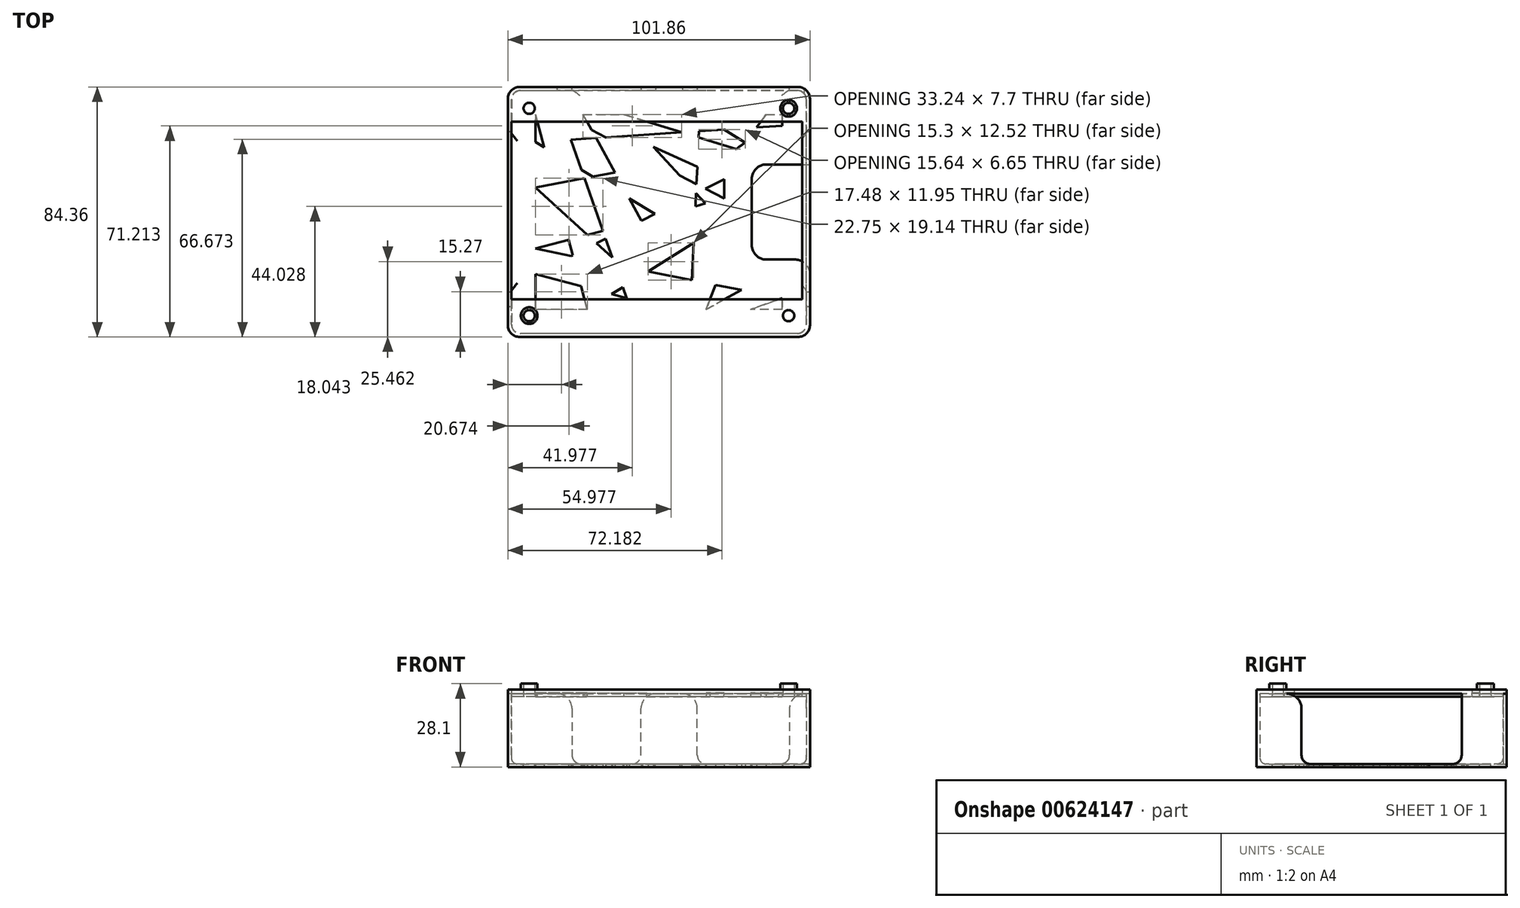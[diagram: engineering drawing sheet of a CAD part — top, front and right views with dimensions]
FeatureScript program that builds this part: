
annotation { "Feature Type Name" : "Feature", "Feature Type Description" : "" }
export const myFeature = defineFeature(function(context is Context, id is Id, definition is map)
    precondition{}
    {
        {
            var Q0;
            Q0=qCreatedBy(makeId("Top.planeOp"),FACE);
            var sketch = newSketch(context, id + "F0", { "sketchPlane" : qUnion([Q0])});
            skPoint(sketch, "E0.middle", {"position": v(0, 0) * mm});
            skLineSegment(sketch, "E1", {"start": v(0, 0) * mm, "end": v(0, -24.25) * mm, "construction": true});
            skLineSegment(sketch, "E2", {"start": v(0, 0) * mm, "end": v(-32.44, 0) * mm, "construction": true});
            skCircle(sketch, "E3", {"center": v(43.73, -34.98) * mm, "radius": 1.9 * mm});
            skCircle(sketch, "E4.MirrorC", {"center": v(-43.73, -34.98) * mm, "radius": 1.9 * mm});
            skCircle(sketch, "E5.MirrorC", {"center": v(-43.73, 34.98) * mm, "radius": 1.9 * mm});
            skCircle(sketch, "E6.MirrorC", {"center": v(43.73, 34.98) * mm, "radius": 1.9 * mm});
            skPoint(sketch, "E0.left.start.orphan", {"position": v(-50, 40) * mm});
            skPoint(sketch, "E0.top.start.orphan", {"position": v(-50, -40) * mm});
            skPoint(sketch, "E0.right.end.orphan", {"position": v(50, -40) * mm});
            skPoint(sketch, "E0.right.start.orphan", {"position": v(50, 40) * mm});
            skSolve(sketch);
        }
        {
            var Q0;
            Q0=qCreatedBy(makeId("Top.planeOp"),FACE);
            var sketch = newSketch(context, id + "F1", { "sketchPlane" : qUnion([Q0])});
            skPoint(sketch, "E7.0", {"position": v(-43.73, 34.98) * mm});
            skPoint(sketch, "E8.0", {"position": v(43.73, 34.98) * mm});
            skPoint(sketch, "E9.0", {"position": v(-43.73, -34.98) * mm});
            skPoint(sketch, "E10.0", {"position": v(43.73, -34.98) * mm});
            skLineSegment(sketch, "E11.0", {"start": v(-49.73, 40.98) * mm, "end": v(49.73, 40.98) * mm});
            skLineSegment(sketch, "E11.1", {"start": v(-49.73, -40.98) * mm, "end": v(-49.73, 40.98) * mm});
            skLineSegment(sketch, "E11.2", {"start": v(49.73, -40.98) * mm, "end": v(-49.73, -40.98) * mm});
            skLineSegment(sketch, "E11.3", {"start": v(49.73, 40.98) * mm, "end": v(49.73, -40.98) * mm});
            skLineSegment(sketch, "E12.0", {"start": v(-50.93, -42.18) * mm, "end": v(-50.93, 42.18) * mm});
            skLineSegment(sketch, "E12.1", {"start": v(50.93, -42.18) * mm, "end": v(-50.93, -42.18) * mm});
            skLineSegment(sketch, "E12.2", {"start": v(50.93, 42.18) * mm, "end": v(50.93, -42.18) * mm});
            skLineSegment(sketch, "E12.3", {"start": v(-50.93, 42.18) * mm, "end": v(50.93, 42.18) * mm});
            skSolve(sketch);
        }
        {
            var Q0;
            Q0=makeQuery(id+"F1.imprint","IMPRINT",FACE,{"disambiguationData":[TD([[makeQuery(id+"F1.imprint","IMPRINT",EDGE,{"derivedFrom":sQuery(id+"F1.wireOp",EDGE,"E11.0")}),-1.0]])]});
            var Q1;
            Q1=makeQuery(id+"F1.imprint","IMPRINT",FACE,{"disambiguationData":[TD([[makeQuery(id+"F1.imprint","IMPRINT",EDGE,{"derivedFrom":sQuery(id+"F1.wireOp",EDGE,"E11.0")}),1.0]])]});
            extrude(context, id + "F2", {"entities" : qUnion([Q0, Q1]), "oppositeDirection" : true, "depth" : 1 * mm, "offsetDistance" : 25 * mm});
        }
        {
            var Q0;
            Q0=makeQuery(id+"F1.imprint","IMPRINT",FACE,{"disambiguationData":[TD([[makeQuery(id+"F1.imprint","IMPRINT",EDGE,{"derivedFrom":sQuery(id+"F1.wireOp",EDGE,"E11.0")}),1.0]])]});
            extrude(context, id + "F3", {"entities" : qUnion([Q0]), "operationType" : NewBodyOperationType.ADD, "depth" : 23.7 * mm, "offsetDistance" : 25 * mm});
        }
        {
            var Q0;
            {var subQ0=sQuery(id+"F1.wireOp",EDGE,"E12.0");Q0=makeQuery(id+"F3.boolean.opBoolean","MERGE",FACE,{"derivedFrom":[makeQuery(id+"F2.opExtrude","SWEPT_FACE",FACE,{"disambiguationData":[OSD([subQ0])]}),makeQuery(id+"F3.opExtrude","SWEPT_FACE",FACE,{"disambiguationData":[OSD([subQ0])]})]});}
            var sketch = newSketch(context, id + "F4", { "sketchPlane" : qUnion([Q0])});
            skLineSegment(sketch, "E13", {"start": v(0, 0) * mm, "end": v(0, 24.76) * mm, "construction": true});
            skPoint(sketch, "E14.0", {"position": v(-40.98, 0) * mm});
            skPoint(sketch, "E15.0", {"position": v(40.98, 23.7) * mm});
            skPoint(sketch, "E16.0", {"position": v(40.98, 0) * mm});
            skPoint(sketch, "E17.0", {"position": v(-40.98, 23.7) * mm});
            skLineSegment(sketch, "E18", {"start": v(-40.98, 23.7) * mm, "end": v(40.98, 0) * mm, "construction": true});
            skLineSegment(sketch, "E19", {"start": v(40.98, 23.7) * mm, "end": v(-40.98, 0) * mm, "construction": true});
            skLineSegment(sketch, "E20.bottom", {"start": v(27, 0) * mm, "end": v(-27, 0) * mm});
            skLineSegment(sketch, "E20.top", {"start": v(27, 24.76) * mm, "end": v(-27, 24.76) * mm});
            skLineSegment(sketch, "E20.left", {"start": v(27, 0) * mm, "end": v(27, 24.76) * mm});
            skLineSegment(sketch, "E20.right", {"start": v(-27, 0) * mm, "end": v(-27, 24.76) * mm});
            skPoint(sketch, "E20.middle", {"position": v(0, 12.38) * mm});
            skSolve(sketch);
        }
        {
            var Q0;
            {var subQ0=sQuery(id+"F4.wireOp",EDGE,"E20.bottom");Q0=makeQuery(id+"F4.imprint","IMPRINT",FACE,{"disambiguationData":[TD([[makeQuery(id+"F4.imprint","IMPRINT",EDGE,{"derivedFrom":subQ0}),-1.0]])]});}
            extrude(context, id + "F5", {"entities" : qUnion([Q0]), "operationType" : NewBodyOperationType.REMOVE, "endBound" : BoundingType.THROUGH_ALL, "oppositeDirection" : true, "depth" : 25 * mm, "offsetDistance" : 25 * mm});
        }
        {
            var Q0;
            {var subQ0=sQuery(id+"F1.wireOp",EDGE,"E12.3");Q0=makeQuery(id+"F3.boolean.opBoolean","MERGE",FACE,{"derivedFrom":[makeQuery(id+"F2.opExtrude","SWEPT_FACE",FACE,{"disambiguationData":[OSD([subQ0])]}),makeQuery(id+"F3.opExtrude","SWEPT_FACE",FACE,{"disambiguationData":[OSD([subQ0])]})]});}
            var sketch = newSketch(context, id + "F6", { "sketchPlane" : qUnion([Q0])});
            skLineSegment(sketch, "E21", {"start": v(-50.93, 11.35) * mm, "end": v(-12.93, 11.35) * mm, "construction": true});
            skLineSegment(sketch, "E22", {"start": v(-50.93, 7.6) * mm, "end": v(6.07, 7.6) * mm, "construction": true});
            skLineSegment(sketch, "E23", {"start": v(-12.93, 11.35) * mm, "end": v(-12.93, 25.37) * mm});
            skLineSegment(sketch, "E24", {"start": v(-12.93, 25.37) * mm, "end": v(-44.03, 25.37) * mm});
            skLineSegment(sketch, "E25", {"start": v(-44.03, 25.37) * mm, "end": v(-44.03, 0) * mm});
            skLineSegment(sketch, "E26", {"start": v(-44.03, 0) * mm, "end": v(-12.93, 0) * mm});
            skLineSegment(sketch, "E27", {"start": v(-12.93, 0) * mm, "end": v(-12.93, 11.35) * mm});
            skLineSegment(sketch, "E28", {"start": v(6.07, 7.6) * mm, "end": v(6.07, 25.85) * mm});
            skLineSegment(sketch, "E29", {"start": v(6.07, 25.85) * mm, "end": v(29.28, 25.85) * mm});
            skLineSegment(sketch, "E30", {"start": v(29.28, 25.85) * mm, "end": v(29.28, 0) * mm});
            skLineSegment(sketch, "E31", {"start": v(29.28, 0) * mm, "end": v(6.07, 0) * mm});
            skLineSegment(sketch, "E32", {"start": v(6.07, 0) * mm, "end": v(6.07, 7.6) * mm});
            skSolve(sketch);
        }
        {
            var Q0;
            Q0 = qSketchRegion(id + "F6", true);
            extrude(context, id + "F7", {"entities" : qUnion([Q0]), "operationType" : NewBodyOperationType.REMOVE, "oppositeDirection" : true, "depth" : 25 * mm, "offsetDistance" : 25 * mm});
        }
        {
            var Q0;
            Q0=makeQuery(id+"F0.imprint","IMPRINT",FACE,{"disambiguationData":[TD([[makeQuery(id+"F0.imprint","IMPRINT",EDGE,{"derivedFrom":sQuery(id+"F0.wireOp",EDGE,"E6.MirrorC")}),-1.0]])]});
            var Q1;
            Q1=makeQuery(id+"F0.imprint","IMPRINT",FACE,{"disambiguationData":[TD([[makeQuery(id+"F0.imprint","IMPRINT",EDGE,{"derivedFrom":sQuery(id+"F0.wireOp",EDGE,"E3")}),1.0]])]});
            var Q2;
            Q2=makeQuery(id+"F0.imprint","IMPRINT",FACE,{"disambiguationData":[TD([[makeQuery(id+"F0.imprint","IMPRINT",EDGE,{"derivedFrom":sQuery(id+"F0.wireOp",EDGE,"E5.MirrorC")}),1.0]])]});
            var Q3;
            Q3=makeQuery(id+"F0.imprint","IMPRINT",FACE,{"disambiguationData":[TD([[makeQuery(id+"F0.imprint","IMPRINT",EDGE,{"derivedFrom":sQuery(id+"F0.wireOp",EDGE,"E4.MirrorC")}),-1.0]])]});
            extrude(context, id + "F8", {"entities" : qUnion([Q0, Q1, Q2, Q3]), "operationType" : NewBodyOperationType.REMOVE, "oppositeDirection" : true, "depth" : 25 * mm, "offsetDistance" : 25 * mm});
        }
        {
            var Q0;
            Q0=makeQuery(id+"F3.opExtrude","SWEPT_EDGE",EDGE,{"disambiguationData":[OSD([sQuery(id+"F1.wireOp",EDGE,"E11.2"),sQuery(id+"F1.wireOp",EDGE,"E11.3")])]});
            var Q1;
            Q1=makeQuery(id+"F3.opExtrude","SWEPT_EDGE",EDGE,{"disambiguationData":[OSD([sQuery(id+"F1.wireOp",EDGE,"E11.1"),sQuery(id+"F1.wireOp",EDGE,"E11.2")])]});
            var Q2;
            Q2=makeQuery(id+"F3.opExtrude","SWEPT_EDGE",EDGE,{"disambiguationData":[OSD([sQuery(id+"F1.wireOp",EDGE,"E11.0"),sQuery(id+"F1.wireOp",EDGE,"E11.1")])]});
            var Q3;
            Q3=makeQuery(id+"F3.opExtrude","SWEPT_EDGE",EDGE,{"disambiguationData":[OSD([sQuery(id+"F1.wireOp",EDGE,"E11.0"),sQuery(id+"F1.wireOp",EDGE,"E11.3")])]});
            fillet(context, id + "F9", {"entities" : qUnion([Q0, Q1, Q2, Q3]), "radius" : 3 * mm, "tangentPropagation" : true, "allowEdgeOverflow" : false});
        }
        {
            var Q0;
            {var subQ0=sQuery(id+"F1.wireOp",EDGE,"E12.3");var subQ1=sQuery(id+"F1.wireOp",EDGE,"E12.0");Q0=makeQuery(id+"F3.boolean.opBoolean","MERGE",EDGE,{"derivedFrom":[makeQuery(id+"F2.opExtrude","SWEPT_EDGE",EDGE,{"disambiguationData":[OSD([subQ1,subQ0])]}),makeQuery(id+"F3.opExtrude","SWEPT_EDGE",EDGE,{"disambiguationData":[OSD([subQ1,subQ0])]})]});}
            var Q1;
            {var subQ0=sQuery(id+"F1.wireOp",EDGE,"E12.1");var subQ1=sQuery(id+"F1.wireOp",EDGE,"E12.0");Q1=makeQuery(id+"F3.boolean.opBoolean","MERGE",EDGE,{"derivedFrom":[makeQuery(id+"F2.opExtrude","SWEPT_EDGE",EDGE,{"disambiguationData":[OSD([subQ1,subQ0])]}),makeQuery(id+"F3.opExtrude","SWEPT_EDGE",EDGE,{"disambiguationData":[OSD([subQ1,subQ0])]})]});}
            var Q2;
            {var subQ0=sQuery(id+"F1.wireOp",EDGE,"E12.2");var subQ1=sQuery(id+"F1.wireOp",EDGE,"E12.1");Q2=makeQuery(id+"F3.boolean.opBoolean","MERGE",EDGE,{"derivedFrom":[makeQuery(id+"F2.opExtrude","SWEPT_EDGE",EDGE,{"disambiguationData":[OSD([subQ1,subQ0])]}),makeQuery(id+"F3.opExtrude","SWEPT_EDGE",EDGE,{"disambiguationData":[OSD([subQ1,subQ0])]})]});}
            var Q3;
            {var subQ0=sQuery(id+"F1.wireOp",EDGE,"E12.3");var subQ1=sQuery(id+"F1.wireOp",EDGE,"E12.2");Q3=makeQuery(id+"F3.boolean.opBoolean","MERGE",EDGE,{"derivedFrom":[makeQuery(id+"F2.opExtrude","SWEPT_EDGE",EDGE,{"disambiguationData":[OSD([subQ1,subQ0])]}),makeQuery(id+"F3.opExtrude","SWEPT_EDGE",EDGE,{"disambiguationData":[OSD([subQ1,subQ0])]})]});}
            fillet(context, id + "F10", {"entities" : qUnion([Q0, Q1, Q2, Q3]), "radius" : 4 * mm, "tangentPropagation" : true, "allowEdgeOverflow" : false});
        }
        {
            var Q0;
            {var subQ0=sQuery(id+"F1.wireOp",EDGE,"E12.0");var subQ1=sQuery(id+"F4.wireOp",EDGE,"E20.bottom");var subQ2=sQuery(id+"F4.wireOp",EDGE,"E20.right");Q0=makeQuery(id+"F5.boolean.opBoolean","COPY",EDGE,{"disambiguationData":[TD([makeQuery(id+"F2.opExtrude","SWEPT_FACE",FACE,{"disambiguationData":[OSD([subQ0])]})])],"derivedFrom":makeQuery(id+"F5.opExtrude","SWEPT_EDGE",EDGE,{"disambiguationData":[OSD([subQ1,subQ2])]})});}
            var Q1;
            Q1=makeQuery(id+"F7.boolean.opBoolean","COPY",EDGE,{"derivedFrom":makeQuery(id+"F7.opExtrude","SWEPT_EDGE",EDGE,{"disambiguationData":[OSD([sQuery(id+"F6.wireOp",EDGE,"E30"),sQuery(id+"F6.wireOp",EDGE,"E31")])]})});
            var Q2;
            Q2=makeQuery(id+"F7.boolean.opBoolean","COPY",EDGE,{"derivedFrom":makeQuery(id+"F7.opExtrude","SWEPT_EDGE",EDGE,{"disambiguationData":[OSD([sQuery(id+"F6.wireOp",EDGE,"E31"),sQuery(id+"F6.wireOp",EDGE,"E32")])]})});
            var Q3;
            Q3=makeQuery(id+"F7.boolean.opBoolean","COPY",EDGE,{"derivedFrom":makeQuery(id+"F7.opExtrude","SWEPT_EDGE",EDGE,{"disambiguationData":[OSD([sQuery(id+"F6.wireOp",EDGE,"E26"),sQuery(id+"F6.wireOp",EDGE,"E27")])]})});
            var Q4;
            Q4=makeQuery(id+"F7.boolean.opBoolean","COPY",EDGE,{"derivedFrom":makeQuery(id+"F7.opExtrude","SWEPT_EDGE",EDGE,{"disambiguationData":[OSD([sQuery(id+"F6.wireOp",EDGE,"E25"),sQuery(id+"F6.wireOp",EDGE,"E26")])]})});
            var Q5;
            {var subQ0=sQuery(id+"F1.wireOp",EDGE,"E12.2");var subQ1=sQuery(id+"F4.wireOp",EDGE,"E20.bottom");var subQ2=sQuery(id+"F4.wireOp",EDGE,"E20.right");Q5=makeQuery(id+"F5.boolean.opBoolean","COPY",EDGE,{"disambiguationData":[TD([makeQuery(id+"F2.opExtrude","SWEPT_FACE",FACE,{"disambiguationData":[OSD([subQ0])]})])],"derivedFrom":makeQuery(id+"F5.opExtrude","SWEPT_EDGE",EDGE,{"disambiguationData":[OSD([subQ1,subQ2])]})});}
            var Q6;
            {var subQ0=sQuery(id+"F1.wireOp",EDGE,"E12.2");var subQ1=sQuery(id+"F4.wireOp",EDGE,"E20.left");var subQ2=sQuery(id+"F4.wireOp",EDGE,"E20.bottom");Q6=makeQuery(id+"F5.boolean.opBoolean","COPY",EDGE,{"disambiguationData":[TD([makeQuery(id+"F2.opExtrude","SWEPT_FACE",FACE,{"disambiguationData":[OSD([subQ0])]})])],"derivedFrom":makeQuery(id+"F5.opExtrude","SWEPT_EDGE",EDGE,{"disambiguationData":[OSD([subQ2,subQ1])]})});}
            var Q7;
            {var subQ0=sQuery(id+"F1.wireOp",EDGE,"E12.0");var subQ1=sQuery(id+"F4.wireOp",EDGE,"E20.left");var subQ2=sQuery(id+"F4.wireOp",EDGE,"E20.bottom");Q7=makeQuery(id+"F5.boolean.opBoolean","COPY",EDGE,{"disambiguationData":[TD([makeQuery(id+"F2.opExtrude","SWEPT_FACE",FACE,{"disambiguationData":[OSD([subQ0])]})])],"derivedFrom":makeQuery(id+"F5.opExtrude","SWEPT_EDGE",EDGE,{"disambiguationData":[OSD([subQ2,subQ1])]})});}
            fillet(context, id + "F11", {"entities" : qUnion([Q0, Q1, Q2, Q3, Q4, Q5, Q6, Q7]), "radius" : 3 * mm, "tangentPropagation" : true, "allowEdgeOverflow" : false});
        }
        {
            var Q0;
            {var subQ1=sQuery(id+"F1.wireOp",EDGE,"E12.2");var subQ2=sQuery(id+"F1.wireOp",EDGE,"E12.0");var subQ3=sQuery(id+"F4.wireOp",EDGE,"E20.left");Q0=makeQuery(id+"F5.boolean.opBoolean","COPY",EDGE,{"disambiguationData":[TD([makeQuery(id+"F2.opExtrude","SWEPT_FACE",FACE,{"disambiguationData":[OSD([subQ1])]})])],"derivedFrom":makeQuery(id+"F5.opExtrude","SWEPT_EDGE",EDGE,{"disambiguationData":[OSD([subQ2,subQ3])]})});}
            var Q1;
            {var subQ1=sQuery(id+"F1.wireOp",EDGE,"E12.2");var subQ2=sQuery(id+"F1.wireOp",EDGE,"E12.0");var subQ3=sQuery(id+"F4.wireOp",EDGE,"E20.right");Q1=makeQuery(id+"F5.boolean.opBoolean","COPY",EDGE,{"disambiguationData":[TD([makeQuery(id+"F2.opExtrude","SWEPT_FACE",FACE,{"disambiguationData":[OSD([subQ1])]})])],"derivedFrom":makeQuery(id+"F5.opExtrude","SWEPT_EDGE",EDGE,{"disambiguationData":[OSD([subQ2,subQ3])]})});}
            var Q2;
            {var subQ0=sQuery(id+"F1.wireOp",EDGE,"E11.0");var subQ1=sQuery(id+"F1.wireOp",EDGE,"E12.2");var subQ2=sQuery(id+"F1.wireOp",EDGE,"E12.3");var subQ3=sQuery(id+"F1.wireOp",EDGE,"E12.0");var subQ4=sQuery(id+"F1.wireOp",EDGE,"E11.1");var subQ5=sQuery(id+"F1.wireOp",EDGE,"E11.3");Q2=makeQuery(id+"F7.boolean.opBoolean","INTERSECT",EDGE,{"derivedFrom":[makeQuery(id+"F5.boolean.opBoolean","SPLIT",FACE,{"disambiguationData":[TD([makeQuery(id+"F2.opExtrude","SWEPT_FACE",FACE,{"disambiguationData":[OSD([subQ2])]})])],"derivedFrom":makeQuery(id+"F3.opExtrude","CAP_FACE",FACE,{"disambiguationData":[OSD([subQ0,subQ4,sQuery(id+"F1.wireOp",EDGE,"E11.2"),subQ5,subQ3,sQuery(id+"F1.wireOp",EDGE,"E12.1"),subQ1,subQ2])],"isStart":false})}),makeQuery(id+"F7.opExtrude","SWEPT_FACE",FACE,{"disambiguationData":[OSD([sQuery(id+"F6.wireOp",EDGE,"E25")])]})]});}
            var Q3;
            {var subQ0=sQuery(id+"F1.wireOp",EDGE,"E11.0");var subQ1=sQuery(id+"F1.wireOp",EDGE,"E12.2");var subQ2=sQuery(id+"F1.wireOp",EDGE,"E12.3");var subQ3=sQuery(id+"F1.wireOp",EDGE,"E12.0");var subQ4=sQuery(id+"F1.wireOp",EDGE,"E11.1");var subQ5=sQuery(id+"F1.wireOp",EDGE,"E11.3");Q3=makeQuery(id+"F7.boolean.opBoolean","INTERSECT",EDGE,{"derivedFrom":[makeQuery(id+"F5.boolean.opBoolean","SPLIT",FACE,{"disambiguationData":[TD([makeQuery(id+"F2.opExtrude","SWEPT_FACE",FACE,{"disambiguationData":[OSD([subQ2])]})])],"derivedFrom":makeQuery(id+"F3.opExtrude","CAP_FACE",FACE,{"disambiguationData":[OSD([subQ0,subQ4,sQuery(id+"F1.wireOp",EDGE,"E11.2"),subQ5,subQ3,sQuery(id+"F1.wireOp",EDGE,"E12.1"),subQ1,subQ2])],"isStart":false})}),makeQuery(id+"F7.opExtrude","SWEPT_FACE",FACE,{"disambiguationData":[OSD([sQuery(id+"F6.wireOp",EDGE,"E23"),sQuery(id+"F6.wireOp",EDGE,"E27")])]})]});}
            var Q4;
            {var subQ0=sQuery(id+"F1.wireOp",EDGE,"E11.0");var subQ1=sQuery(id+"F1.wireOp",EDGE,"E12.2");var subQ2=sQuery(id+"F1.wireOp",EDGE,"E12.3");var subQ3=sQuery(id+"F1.wireOp",EDGE,"E12.0");var subQ4=sQuery(id+"F1.wireOp",EDGE,"E11.1");var subQ5=sQuery(id+"F1.wireOp",EDGE,"E11.3");Q4=makeQuery(id+"F7.boolean.opBoolean","INTERSECT",EDGE,{"derivedFrom":[makeQuery(id+"F5.boolean.opBoolean","SPLIT",FACE,{"disambiguationData":[TD([makeQuery(id+"F2.opExtrude","SWEPT_FACE",FACE,{"disambiguationData":[OSD([subQ2])]})])],"derivedFrom":makeQuery(id+"F3.opExtrude","CAP_FACE",FACE,{"disambiguationData":[OSD([subQ0,subQ4,sQuery(id+"F1.wireOp",EDGE,"E11.2"),subQ5,subQ3,sQuery(id+"F1.wireOp",EDGE,"E12.1"),subQ1,subQ2])],"isStart":false})}),makeQuery(id+"F7.opExtrude","SWEPT_FACE",FACE,{"disambiguationData":[OSD([sQuery(id+"F6.wireOp",EDGE,"E28"),sQuery(id+"F6.wireOp",EDGE,"E32")])]})]});}
            var Q5;
            {var subQ0=sQuery(id+"F1.wireOp",EDGE,"E11.0");var subQ1=sQuery(id+"F1.wireOp",EDGE,"E12.2");var subQ2=sQuery(id+"F1.wireOp",EDGE,"E12.3");var subQ3=sQuery(id+"F1.wireOp",EDGE,"E12.0");var subQ4=sQuery(id+"F1.wireOp",EDGE,"E11.1");var subQ5=sQuery(id+"F1.wireOp",EDGE,"E11.3");Q5=makeQuery(id+"F7.boolean.opBoolean","INTERSECT",EDGE,{"derivedFrom":[makeQuery(id+"F5.boolean.opBoolean","SPLIT",FACE,{"disambiguationData":[TD([makeQuery(id+"F2.opExtrude","SWEPT_FACE",FACE,{"disambiguationData":[OSD([subQ2])]})])],"derivedFrom":makeQuery(id+"F3.opExtrude","CAP_FACE",FACE,{"disambiguationData":[OSD([subQ0,subQ4,sQuery(id+"F1.wireOp",EDGE,"E11.2"),subQ5,subQ3,sQuery(id+"F1.wireOp",EDGE,"E12.1"),subQ1,subQ2])],"isStart":false})}),makeQuery(id+"F7.opExtrude","SWEPT_FACE",FACE,{"disambiguationData":[OSD([sQuery(id+"F6.wireOp",EDGE,"E30")])]})]});}
            var Q6;
            {var subQ0=sQuery(id+"F1.wireOp",EDGE,"E12.0");var subQ2=sQuery(id+"F4.wireOp",EDGE,"E20.right");Q6=makeQuery(id+"F5.boolean.opBoolean","COPY",EDGE,{"disambiguationData":[TD([makeQuery(id+"F2.opExtrude","SWEPT_FACE",FACE,{"disambiguationData":[OSD([subQ0])]})])],"derivedFrom":makeQuery(id+"F5.opExtrude","SWEPT_EDGE",EDGE,{"disambiguationData":[OSD([subQ0,subQ2])]})});}
            var Q7;
            {var subQ0=sQuery(id+"F1.wireOp",EDGE,"E12.0");var subQ2=sQuery(id+"F4.wireOp",EDGE,"E20.left");Q7=makeQuery(id+"F5.boolean.opBoolean","COPY",EDGE,{"disambiguationData":[TD([makeQuery(id+"F2.opExtrude","SWEPT_FACE",FACE,{"disambiguationData":[OSD([subQ0])]})])],"derivedFrom":makeQuery(id+"F5.opExtrude","SWEPT_EDGE",EDGE,{"disambiguationData":[OSD([subQ0,subQ2])]})});}
            fillet(context, id + "F12", {"entities" : qUnion([Q0, Q1, Q2, Q3, Q4, Q5, Q6, Q7]), "radius" : 5 * mm, "tangentPropagation" : true, "allowEdgeOverflow" : false});
        }
        {
            var Q0;
            Q0=makeQuery(id+"F2.opExtrude","CAP_FACE",FACE,{"disambiguationData":[OSD([sQuery(id+"F1.wireOp",EDGE,"E12.0"),sQuery(id+"F1.wireOp",EDGE,"E12.1"),sQuery(id+"F1.wireOp",EDGE,"E12.2"),sQuery(id+"F1.wireOp",EDGE,"E12.3")])],"isStart":false});
            var sketch = newSketch(context, id + "F13", { "sketchPlane" : qUnion([Q0])});
            skLineSegment(sketch, "E33.top", {"start": v(50.93, 16.06) * mm, "end": v(31.3, 16.06) * mm});
            skLineSegment(sketch, "E33.left", {"start": v(50.93, 0) * mm, "end": v(50.93, 16.06) * mm});
            skLineSegment(sketch, "E33.right", {"start": v(31.3, 0) * mm, "end": v(31.3, 16.06) * mm});
            skLineSegment(sketch, "E34.MirrorCS", {"start": v(50.93, 0) * mm, "end": v(50.93, -16.06) * mm});
            skLineSegment(sketch, "E35.MirrorCS", {"start": v(50.93, -16.06) * mm, "end": v(31.3, -16.06) * mm});
            skLineSegment(sketch, "E36.MirrorCS", {"start": v(31.3, 0) * mm, "end": v(31.3, -16.06) * mm});
            skSolve(sketch);
        }
        {
            var Q0;
            Q0=makeQuery(id+"F13.imprint","IMPRINT",FACE,{"disambiguationData":[TD([[makeQuery(id+"F13.imprint","IMPRINT",EDGE,{"derivedFrom":sQuery(id+"F13.wireOp",EDGE,"E33.top")}),1.0]])]});
            extrude(context, id + "F14", {"entities" : qUnion([Q0]), "operationType" : NewBodyOperationType.REMOVE, "oppositeDirection" : true, "depth" : 25 * mm, "offsetDistance" : 25 * mm});
        }
        {
            var Q0;
            Q0=makeQuery(id+"F14.boolean.opBoolean","COPY",EDGE,{"derivedFrom":makeQuery(id+"F14.opExtrude","SWEPT_EDGE",EDGE,{"disambiguationData":[OSD([sQuery(id+"F1.wireOp",EDGE,"E12.2"),sQuery(id+"F13.wireOp",EDGE,"E33.top"),sQuery(id+"F13.wireOp",EDGE,"E33.left")])]})});
            var Q1;
            Q1=makeQuery(id+"F14.boolean.opBoolean","COPY",EDGE,{"derivedFrom":makeQuery(id+"F14.opExtrude","SWEPT_EDGE",EDGE,{"disambiguationData":[OSD([sQuery(id+"F1.wireOp",EDGE,"E12.2"),sQuery(id+"F13.wireOp",EDGE,"E34.MirrorCS"),sQuery(id+"F13.wireOp",EDGE,"E35.MirrorCS")])]})});
            var Q2;
            Q2=makeQuery(id+"F14.boolean.opBoolean","COPY",EDGE,{"derivedFrom":makeQuery(id+"F14.opExtrude","SWEPT_EDGE",EDGE,{"disambiguationData":[OSD([sQuery(id+"F13.wireOp",EDGE,"E33.top"),sQuery(id+"F13.wireOp",EDGE,"E33.right")])]})});
            var Q3;
            Q3=makeQuery(id+"F14.boolean.opBoolean","COPY",EDGE,{"derivedFrom":makeQuery(id+"F14.opExtrude","SWEPT_EDGE",EDGE,{"disambiguationData":[OSD([sQuery(id+"F13.wireOp",EDGE,"E35.MirrorCS"),sQuery(id+"F13.wireOp",EDGE,"E36.MirrorCS")])]})});
            fillet(context, id + "F15", {"entities" : qUnion([Q0, Q1, Q2, Q3]), "radius" : 5 * mm, "tangentPropagation" : true, "allowEdgeOverflow" : false});
        }
        {
            var Q0;
            Q0=qCreatedBy(makeId("Top.planeOp"),FACE);
            cPlane(context, id + "F16", {"entities" : qUnion([Q0]), "cplaneType" : CPlaneType.OFFSET, "offset" : 23.7 * mm, "width" : 150 * mm, "height" : 150 * mm});
        }
        {
            var Q0;
            Q0=qCreatedBy(id+"F16.planeOp",FACE);
            var sketch = newSketch(context, id + "F17", { "sketchPlane" : qUnion([Q0])});
            skLineSegment(sketch, "E37.0", {"start": v(50.93, -32) * mm, "end": v(50.93, -38.18) * mm});
            skArc(sketch, "E38.0", {"start": v(46.93, -42.18) * mm, "mid": v(49.76, -41.01) * mm, "end": v(50.93, -38.18) * mm});
            skLineSegment(sketch, "E39.0", {"start": v(46.93, -42.18) * mm, "end": v(-46.93, -42.18) * mm});
            skArc(sketch, "E40.0", {"start": v(-50.93, -38.18) * mm, "mid": v(-49.76, -41.01) * mm, "end": v(-46.93, -42.18) * mm});
            skLineSegment(sketch, "E41.0", {"start": v(-50.93, -38.18) * mm, "end": v(-50.93, -32) * mm});
            skLineSegment(sketch, "E42.0", {"start": v(-49.73, -37.98) * mm, "end": v(-49.73, -32) * mm});
            skArc(sketch, "E43.0", {"start": v(-46.73, -40.98) * mm, "mid": v(-48.85, -40.1) * mm, "end": v(-49.73, -37.98) * mm});
            skLineSegment(sketch, "E44.0", {"start": v(46.73, -40.98) * mm, "end": v(-46.73, -40.98) * mm});
            skArc(sketch, "E45.0", {"start": v(49.73, -37.98) * mm, "mid": v(48.85, -40.1) * mm, "end": v(46.73, -40.98) * mm});
            skLineSegment(sketch, "E46.0", {"start": v(49.73, -32) * mm, "end": v(49.73, -37.98) * mm});
            skLineSegment(sketch, "E47.0", {"start": v(49.73, 37.98) * mm, "end": v(49.73, 32) * mm});
            skLineSegment(sketch, "E48.0", {"start": v(50.93, 38.18) * mm, "end": v(50.93, 32) * mm});
            skArc(sketch, "E49.0", {"start": v(49.03, 39.9) * mm, "mid": v(49.55, 39) * mm, "end": v(49.73, 37.98) * mm});
            skArc(sketch, "E50.0", {"start": v(49.03, 39.9) * mm, "mid": v(48, 40.7) * mm, "end": v(46.73, 40.98) * mm});
            skLineSegment(sketch, "E51.0", {"start": v(46.73, 40.98) * mm, "end": v(44.03, 40.98) * mm});
            skLineSegment(sketch, "E52.0", {"start": v(44.03, 42.18) * mm, "end": v(46.93, 42.18) * mm});
            skArc(sketch, "E53.0", {"start": v(49.03, 41.58) * mm, "mid": v(48.02, 42.03) * mm, "end": v(46.93, 42.18) * mm});
            skArc(sketch, "E54.0", {"start": v(50.93, 38.18) * mm, "mid": v(50.42, 40.13) * mm, "end": v(49.03, 41.58) * mm});
            skLineSegment(sketch, "E55.0", {"start": v(50.93, 32) * mm, "end": v(50.93, 27) * mm});
            skLineSegment(sketch, "E56.0", {"start": v(49.73, 27) * mm, "end": v(49.73, 32) * mm});
            skLineSegment(sketch, "E57.0", {"start": v(-46.73, 40.98) * mm, "end": v(-34.28, 40.98) * mm});
            skLineSegment(sketch, "E58.0", {"start": v(-46.93, 42.18) * mm, "end": v(-34.28, 42.18) * mm});
            skArc(sketch, "E59.0", {"start": v(-46.93, 42.18) * mm, "mid": v(-49.76, 41.01) * mm, "end": v(-50.93, 38.18) * mm});
            skArc(sketch, "E60.0", {"start": v(-49.73, 37.98) * mm, "mid": v(-48.85, 40.1) * mm, "end": v(-46.73, 40.98) * mm});
            skLineSegment(sketch, "E61.0", {"start": v(-49.73, 32) * mm, "end": v(-49.73, 37.98) * mm});
            skLineSegment(sketch, "E62.0", {"start": v(-50.93, 32) * mm, "end": v(-50.93, 38.18) * mm});
            skLineSegment(sketch, "E63", {"start": v(49.73, -32) * mm, "end": v(49.73, 27) * mm});
            skLineSegment(sketch, "E64", {"start": v(50.93, -32) * mm, "end": v(50.93, 27) * mm});
            skLineSegment(sketch, "E65", {"start": v(44.03, 40.98) * mm, "end": v(-34.28, 40.98) * mm});
            skLineSegment(sketch, "E66", {"start": v(44.03, 42.18) * mm, "end": v(-34.28, 42.18) * mm});
            skLineSegment(sketch, "E67", {"start": v(-49.73, 32) * mm, "end": v(-49.73, -32) * mm});
            skLineSegment(sketch, "E68", {"start": v(-50.93, 32) * mm, "end": v(-50.93, -32) * mm});
            skCircle(sketch, "E69.0", {"center": v(-43.73, -34.98) * mm, "radius": 1.9 * mm});
            skCircle(sketch, "E70.0", {"center": v(-43.73, 34.98) * mm, "radius": 1.9 * mm});
            skCircle(sketch, "E71.0", {"center": v(43.73, -34.98) * mm, "radius": 1.9 * mm});
            skCircle(sketch, "E72.0", {"center": v(43.73, 34.98) * mm, "radius": 1.9 * mm});
            skLineSegment(sketch, "E73", {"start": v(43.73, 34.98) * mm, "end": v(43.73, 30.48) * mm, "construction": true});
            skLineSegment(sketch, "E74", {"start": v(43.73, 30.48) * mm, "end": v(48.29, 30.48) * mm, "construction": true});
            skLineSegment(sketch, "E75", {"start": v(48.29, 30.48) * mm, "end": v(-49.73, 30.48) * mm});
            skLineSegment(sketch, "E76", {"start": v(-49.73, 30.48) * mm, "end": v(-49.73, -29.52) * mm});
            skLineSegment(sketch, "E77", {"start": v(-49.73, -29.52) * mm, "end": v(48.29, -29.52) * mm});
            skLineSegment(sketch, "E78", {"start": v(48.29, -29.52) * mm, "end": v(48.29, 30.48) * mm});
            skSolve(sketch);
        }
        {
            var Q0;
            {var subQ2=sQuery(id+"F17.wireOp",EDGE,"E42.0");Q0=makeQuery(id+"F17.imprint","IMPRINT",FACE,{"disambiguationData":[TD([[makeQuery(id+"F17.imprint","IMPRINT",EDGE,{"derivedFrom":subQ2}),-1.0]])]});}
            var Q1;
            Q1=makeQuery(id+"F17.imprint","IMPRINT",FACE,{"disambiguationData":[TD([[makeQuery(id+"F17.imprint","IMPRINT",EDGE,{"derivedFrom":sQuery(id+"F17.wireOp",EDGE,"E37.0")}),-1.0]])]});
            extrude(context, id + "F18", {"entities" : qUnion([Q0, Q1]), "depth" : 3.4 * mm, "offsetDistance" : 25 * mm});
        }
        {
            var Q0;
            {var subQ2=sQuery(id+"F17.wireOp",EDGE,"E42.0");Q0=makeQuery(id+"F17.imprint","IMPRINT",FACE,{"disambiguationData":[TD([[makeQuery(id+"F17.imprint","IMPRINT",EDGE,{"derivedFrom":subQ2}),-1.0]])]});}
            extrude(context, id + "F19", {"entities" : qUnion([Q0]), "operationType" : NewBodyOperationType.ADD, "oppositeDirection" : true, "depth" : 1 * mm, "offsetDistance" : 25 * mm, "hasDraft" : true, "draftAngle" : 4 * degree, "draftPullDirection" : true});
        }
        {
            var Q0;
            Q0=makeQuery(id+"F18.opExtrude","CAP_FACE",FACE,{"disambiguationData":[OSD([sQuery(id+"F17.wireOp",EDGE,"E37.0"),sQuery(id+"F17.wireOp",EDGE,"E38.0"),sQuery(id+"F17.wireOp",EDGE,"E39.0"),sQuery(id+"F17.wireOp",EDGE,"E40.0"),sQuery(id+"F17.wireOp",EDGE,"E41.0"),sQuery(id+"F17.wireOp",EDGE,"E48.0"),sQuery(id+"F17.wireOp",EDGE,"E52.0"),sQuery(id+"F17.wireOp",EDGE,"E53.0"),sQuery(id+"F17.wireOp",EDGE,"E54.0"),sQuery(id+"F17.wireOp",EDGE,"E55.0"),sQuery(id+"F17.wireOp",EDGE,"E58.0"),sQuery(id+"F17.wireOp",EDGE,"E59.0"),sQuery(id+"F17.wireOp",EDGE,"E62.0"),sQuery(id+"F17.wireOp",EDGE,"E64"),sQuery(id+"F17.wireOp",EDGE,"E66"),sQuery(id+"F17.wireOp",EDGE,"E68"),sQuery(id+"F17.wireOp",EDGE,"E69.0"),sQuery(id+"F17.wireOp",EDGE,"E70.0"),sQuery(id+"F17.wireOp",EDGE,"E71.0"),sQuery(id+"F17.wireOp",EDGE,"E72.0"),sQuery(id+"F17.wireOp",EDGE,"E75"),sQuery(id+"F17.wireOp",EDGE,"E76"),sQuery(id+"F17.wireOp",EDGE,"E77"),sQuery(id+"F17.wireOp",EDGE,"E78")])],"isStart":false});
            var sketch = newSketch(context, id + "F20", { "sketchPlane" : qUnion([Q0])});
            skCircle(sketch, "E79", {"center": v(-43.73, 34.98) * mm, "radius": 2.8 * mm});
            skLineSegment(sketch, "E80", {"start": v(0, 0) * mm, "end": v(0, 13.28) * mm, "construction": true});
            skLineSegment(sketch, "E81", {"start": v(0, 0) * mm, "end": v(-20.42, 0) * mm, "construction": true});
            skCircle(sketch, "E82.MirrorC", {"center": v(43.73, 34.98) * mm, "radius": 2.8 * mm});
            skCircle(sketch, "E83.MirrorC", {"center": v(-43.73, -34.98) * mm, "radius": 2.8 * mm});
            skCircle(sketch, "E84.MirrorC", {"center": v(43.73, -34.98) * mm, "radius": 2.8 * mm});
            skSolve(sketch);
        }
        {
            var Q0;
            Q0=makeQuery(id+"F20.imprint","IMPRINT",FACE,{"disambiguationData":[TD([[makeQuery(id+"F20.imprint","IMPRINT",EDGE,{"derivedFrom":sQuery(id+"F20.wireOp",EDGE,"E79")}),1.0]])]});
            var Q1;
            Q1=makeQuery(id+"F20.imprint","IMPRINT",FACE,{"disambiguationData":[TD([[makeQuery(id+"F20.imprint","IMPRINT",EDGE,{"derivedFrom":sQuery(id+"F20.wireOp",EDGE,"E82.MirrorC")}),-1.0]])]});
            var Q2;
            Q2=makeQuery(id+"F20.imprint","IMPRINT",FACE,{"disambiguationData":[TD([[makeQuery(id+"F20.imprint","IMPRINT",EDGE,{"derivedFrom":sQuery(id+"F20.wireOp",EDGE,"E84.MirrorC")}),1.0]])]});
            var Q3;
            Q3=makeQuery(id+"F20.imprint","IMPRINT",FACE,{"disambiguationData":[TD([[makeQuery(id+"F20.imprint","IMPRINT",EDGE,{"derivedFrom":sQuery(id+"F20.wireOp",EDGE,"E83.MirrorC")}),-1.0]])]});
            var Q4;
            Q4=sQuery(id+"F20.wireOp",EDGE,"E79");
            var Q5;
            Q5=sQuery(id+"F20.wireOp",EDGE,"E82.MirrorC");
            var Q6;
            Q6=sQuery(id+"F20.wireOp",EDGE,"E84.MirrorC");
            var Q7;
            Q7=sQuery(id+"F20.wireOp",EDGE,"E83.MirrorC");
            extrude(context, id + "F21", {"entities" : qUnion([Q0, Q1, Q2, Q3]), "operationType" : NewBodyOperationType.REMOVE, "surfaceEntities" : qUnion([Q4, Q5, Q6, Q7]), "oppositeDirection" : true, "depth" : 2 * mm, "offsetDistance" : 25 * mm});
        }
        {
            var Q0;
            Q0=makeQuery(id+"F2.opExtrude","CAP_FACE",FACE,{"disambiguationData":[OSD([sQuery(id+"F1.wireOp",EDGE,"E12.0"),sQuery(id+"F1.wireOp",EDGE,"E12.1"),sQuery(id+"F1.wireOp",EDGE,"E12.2"),sQuery(id+"F1.wireOp",EDGE,"E12.3")])],"isStart":false});
            var sketch = newSketch(context, id + "F22", { "sketchPlane" : qUnion([Q0])});
            skLineSegment(sketch, "E85.0", {"start": v(-41.63, 32.88) * mm, "end": v(-41.63, -32.88) * mm});
            skLineSegment(sketch, "E85.1", {"start": v(41.63, 32.88) * mm, "end": v(-41.63, 32.88) * mm});
            skLineSegment(sketch, "E85.2", {"start": v(-41.63, -32.88) * mm, "end": v(41.63, -32.88) * mm});
            skLineSegment(sketch, "E85.3", {"start": v(41.63, 25.36) * mm, "end": v(41.63, 32.88) * mm});
            skLineSegment(sketch, "E85.4", {"start": v(41.63, 25.36) * mm, "end": v(36.3, 25.36) * mm});
            skArc(sketch, "E85.5", {"start": v(22, 11.06) * mm, "mid": v(26.19, 21.17) * mm, "end": v(36.3, 25.36) * mm});
            skLineSegment(sketch, "E85.6", {"start": v(41.63, -32.88) * mm, "end": v(41.63, -25.36) * mm});
            skLineSegment(sketch, "E85.7", {"start": v(41.63, -25.36) * mm, "end": v(36.3, -25.36) * mm});
            skArc(sketch, "E85.8", {"start": v(36.3, -25.36) * mm, "mid": v(26.19, -21.17) * mm, "end": v(22, -11.06) * mm});
            skLineSegment(sketch, "E85.9", {"start": v(22, -11.06) * mm, "end": v(22, 11.06) * mm});
            skLineSegment(sketch, "E86", {"start": v(-41.63, -32.88) * mm, "end": v(-24.14, 32.88) * mm});
            skLineSegment(sketch, "E87", {"start": v(-24.14, 32.88) * mm, "end": v(22, 4) * mm});
            skLineSegment(sketch, "E88", {"start": v(22, 4) * mm, "end": v(-11.85, -32.88) * mm});
            skLineSegment(sketch, "E89", {"start": v(-11.85, -32.88) * mm, "end": v(26.19, -21.17) * mm});
            skLineSegment(sketch, "E90", {"start": v(26.19, -21.17) * mm, "end": v(-41.63, -8.29) * mm});
            skLineSegment(sketch, "E91", {"start": v(-41.63, -8.29) * mm, "end": v(3.47, 32.88) * mm});
            skLineSegment(sketch, "E92", {"start": v(3.47, 32.88) * mm, "end": v(-41.63, 20.94) * mm});
            skLineSegment(sketch, "E93", {"start": v(-41.63, 20.94) * mm, "end": v(22, -11.06) * mm});
            skLineSegment(sketch, "E94", {"start": v(22, -11.06) * mm, "end": v(-25.57, -32.88) * mm});
            skLineSegment(sketch, "E95", {"start": v(-25.57, -32.88) * mm, "end": v(10.6, 32.88) * mm});
            skLineSegment(sketch, "E96", {"start": v(10.6, 32.88) * mm, "end": v(13.8, -32.88) * mm});
            skLineSegment(sketch, "E97", {"start": v(13.8, -32.88) * mm, "end": v(29.07, -23.4) * mm});
            skLineSegment(sketch, "E98", {"start": v(29.07, -23.4) * mm, "end": v(36.08, -32.88) * mm});
            skLineSegment(sketch, "E99", {"start": v(36.08, -32.88) * mm, "end": v(41.63, -29.12) * mm});
            skLineSegment(sketch, "E100", {"start": v(41.63, -29.12) * mm, "end": v(-41.63, -23.61) * mm});
            skLineSegment(sketch, "E101", {"start": v(-41.63, -23.61) * mm, "end": v(22.58, 15.1) * mm});
            skLineSegment(sketch, "E102", {"start": v(22.58, 15.1) * mm, "end": v(15.95, 32.88) * mm});
            skLineSegment(sketch, "E103", {"start": v(15.95, 32.88) * mm, "end": v(31.28, 24.45) * mm});
            skLineSegment(sketch, "E104", {"start": v(31.28, 24.45) * mm, "end": v(30.87, 32.88) * mm});
            skLineSegment(sketch, "E105", {"start": v(30.87, 32.88) * mm, "end": v(41.63, 29.12) * mm});
            skLineSegment(sketch, "E106", {"start": v(41.63, 29.12) * mm, "end": v(-41.63, 12.38) * mm});
            skLineSegment(sketch, "E107", {"start": v(-41.63, 12.38) * mm, "end": v(22, -4.53) * mm});
            skLineSegment(sketch, "E108", {"start": v(22, -4.53) * mm, "end": v(-32.7, -32.88) * mm});
            skLineSegment(sketch, "E109", {"start": v(-32.7, -32.88) * mm, "end": v(-9.53, 32.88) * mm});
            skSolve(sketch);
        }
        {
            var Q0;
            {var subQ0=sQuery(id+"F22.wireOp",EDGE,"E107");var subQ1=sQuery(id+"F22.wireOp",EDGE,"E86");var subQ2=makeQuery(id+"F22.imprint","INTERSECT",VERTEX,{"derivedFrom":[subQ1,subQ0]});Q0=makeQuery(id+"F22.imprint","IMPRINT",FACE,{"disambiguationData":[TD([[makeQuery(id+"F22.imprint","IMPRINT",EDGE,{"disambiguationData":[TD([[subQ2,-1.0]])],"derivedFrom":subQ1}),1.0]])]});}
            var Q1;
            {var subQ0=sQuery(id+"F22.wireOp",EDGE,"E92");var subQ1=sQuery(id+"F22.wireOp",EDGE,"E87");var subQ2=makeQuery(id+"F22.imprint","INTERSECT",VERTEX,{"derivedFrom":[subQ1,subQ0]});Q1=makeQuery(id+"F22.imprint","IMPRINT",FACE,{"disambiguationData":[TD([[makeQuery(id+"F22.imprint","IMPRINT",EDGE,{"disambiguationData":[TD([[subQ2,-1.0]])],"derivedFrom":subQ1}),1.0]])]});}
            var Q2;
            {var subQ0=sQuery(id+"F22.wireOp",EDGE,"E85.1");var subQ1=sQuery(id+"F22.wireOp",EDGE,"E85.0");var subQ2=makeQuery(id+"F22.imprint","INTERSECT",VERTEX,{"derivedFrom":[subQ1,subQ0]});Q2=makeQuery(id+"F22.imprint","IMPRINT",FACE,{"disambiguationData":[TD([[makeQuery(id+"F22.imprint","IMPRINT",EDGE,{"disambiguationData":[TD([[subQ2,-1.0]])],"derivedFrom":subQ1}),1.0]])]});}
            var Q3;
            {var subQ0=sQuery(id+"F22.wireOp",EDGE,"E93");var subQ1=sQuery(id+"F22.wireOp",EDGE,"E91");var subQ2=makeQuery(id+"F22.imprint","INTERSECT",VERTEX,{"derivedFrom":[subQ1,subQ0]});Q3=makeQuery(id+"F22.imprint","IMPRINT",FACE,{"disambiguationData":[TD([[makeQuery(id+"F22.imprint","IMPRINT",EDGE,{"disambiguationData":[TD([[subQ2,-1.0]])],"derivedFrom":subQ1}),-1.0]])]});}
            var Q4;
            {var subQ5=sQuery(id+"F22.wireOp",EDGE,"E90");var subQ6=sQuery(id+"F22.wireOp",EDGE,"E86");var subQ7=makeQuery(id+"F22.imprint","INTERSECT",VERTEX,{"derivedFrom":[subQ6,subQ5]});Q4=makeQuery(id+"F22.imprint","IMPRINT",FACE,{"disambiguationData":[TD([[makeQuery(id+"F22.imprint","IMPRINT",EDGE,{"disambiguationData":[TD([[subQ7,-1.0]])],"derivedFrom":subQ6}),-1.0]])]});}
            var Q5;
            {var subQ0=sQuery(id+"F22.wireOp",EDGE,"E95");var subQ1=sQuery(id+"F22.wireOp",EDGE,"E90");var subQ2=makeQuery(id+"F22.imprint","INTERSECT",VERTEX,{"derivedFrom":[subQ1,subQ0]});Q5=makeQuery(id+"F22.imprint","IMPRINT",FACE,{"disambiguationData":[TD([[makeQuery(id+"F22.imprint","IMPRINT",EDGE,{"disambiguationData":[TD([[subQ2,-1.0]])],"derivedFrom":subQ1}),1.0]])]});}
            var Q6;
            {var subQ0=sQuery(id+"F22.wireOp",EDGE,"E107");var subQ1=sQuery(id+"F22.wireOp",EDGE,"E93");var subQ2=makeQuery(id+"F22.imprint","INTERSECT",VERTEX,{"derivedFrom":[subQ1,subQ0]});Q6=makeQuery(id+"F22.imprint","IMPRINT",FACE,{"disambiguationData":[TD([[makeQuery(id+"F22.imprint","IMPRINT",EDGE,{"disambiguationData":[TD([[subQ2,-1.0]])],"derivedFrom":subQ1}),-1.0]])]});}
            var Q7;
            {var subQ1=sQuery(id+"F22.wireOp",EDGE,"E94");var subQ3=sQuery(id+"F22.wireOp",EDGE,"E100");var subQ4=makeQuery(id+"F22.imprint","INTERSECT",VERTEX,{"derivedFrom":[subQ1,subQ3]});Q7=makeQuery(id+"F22.imprint","IMPRINT",FACE,{"disambiguationData":[TD([[makeQuery(id+"F22.imprint","IMPRINT",EDGE,{"disambiguationData":[TD([[subQ4,-1.0]])],"derivedFrom":subQ3}),1.0]])]});}
            var Q8;
            {var subQ0=sQuery(id+"F22.wireOp",EDGE,"E86");var subQ3=sQuery(id+"F22.wireOp",EDGE,"E100");var subQ5=makeQuery(id+"F22.imprint","INTERSECT",VERTEX,{"derivedFrom":[subQ0,subQ3]});Q8=makeQuery(id+"F22.imprint","IMPRINT",FACE,{"disambiguationData":[TD([[makeQuery(id+"F22.imprint","IMPRINT",EDGE,{"disambiguationData":[TD([[subQ5,1.0]])],"derivedFrom":subQ0}),1.0]])]});}
            var Q9;
            {var subQ0=sQuery(id+"F22.wireOp",EDGE,"E100");var subQ1=sQuery(id+"F22.wireOp",EDGE,"E86");var subQ2=makeQuery(id+"F22.imprint","INTERSECT",VERTEX,{"derivedFrom":[subQ1,subQ0]});Q9=makeQuery(id+"F22.imprint","IMPRINT",FACE,{"disambiguationData":[TD([[makeQuery(id+"F22.imprint","IMPRINT",EDGE,{"disambiguationData":[TD([[subQ2,-1.0]])],"derivedFrom":subQ1}),1.0]])]});}
            var Q10;
            {var subQ0=sQuery(id+"F22.wireOp",EDGE,"E88");var subQ5=sQuery(id+"F22.wireOp",EDGE,"E100");var subQ6=makeQuery(id+"F22.imprint","INTERSECT",VERTEX,{"derivedFrom":[subQ0,subQ5]});Q10=makeQuery(id+"F22.imprint","IMPRINT",FACE,{"disambiguationData":[TD([[makeQuery(id+"F22.imprint","IMPRINT",EDGE,{"disambiguationData":[TD([[subQ6,-1.0]])],"derivedFrom":subQ5}),1.0]])]});}
            var Q11;
            {var subQ1=sQuery(id+"F22.wireOp",EDGE,"E88");var subQ3=sQuery(id+"F22.wireOp",EDGE,"E100");var subQ4=makeQuery(id+"F22.imprint","INTERSECT",VERTEX,{"derivedFrom":[subQ1,subQ3]});Q11=makeQuery(id+"F22.imprint","IMPRINT",FACE,{"disambiguationData":[TD([[makeQuery(id+"F22.imprint","IMPRINT",EDGE,{"disambiguationData":[TD([[subQ4,1.0]])],"derivedFrom":subQ3}),1.0]])]});}
            var Q12;
            {var subQ0=sQuery(id+"F22.wireOp",EDGE,"E90");var subQ1=sQuery(id+"F22.wireOp",EDGE,"E88");var subQ2=makeQuery(id+"F22.imprint","INTERSECT",VERTEX,{"derivedFrom":[subQ1,subQ0]});Q12=makeQuery(id+"F22.imprint","IMPRINT",FACE,{"disambiguationData":[TD([[makeQuery(id+"F22.imprint","IMPRINT",EDGE,{"disambiguationData":[TD([[subQ2,-1.0]])],"derivedFrom":subQ1}),1.0]])]});}
            var Q13;
            {var subQ3=sQuery(id+"F22.wireOp",EDGE,"E108");var subQ7=sQuery(id+"F22.wireOp",EDGE,"E88");var subQ9=makeQuery(id+"F22.imprint","INTERSECT",VERTEX,{"derivedFrom":[subQ7,subQ3]});Q13=makeQuery(id+"F22.imprint","IMPRINT",FACE,{"disambiguationData":[TD([[makeQuery(id+"F22.imprint","IMPRINT",EDGE,{"disambiguationData":[TD([[subQ9,-1.0]])],"derivedFrom":subQ7}),1.0]])]});}
            var Q14;
            {var subQ5=sQuery(id+"F22.wireOp",EDGE,"E96");var subQ6=sQuery(id+"F22.wireOp",EDGE,"E89");var subQ7=makeQuery(id+"F22.imprint","INTERSECT",VERTEX,{"derivedFrom":[subQ6,subQ5]});Q14=makeQuery(id+"F22.imprint","IMPRINT",FACE,{"disambiguationData":[TD([[makeQuery(id+"F22.imprint","IMPRINT",EDGE,{"disambiguationData":[TD([[subQ7,-1.0]])],"derivedFrom":subQ5}),1.0]])]});}
            var Q15;
            {var subQ0=sQuery(id+"F22.wireOp",EDGE,"E99");Q15=makeQuery(id+"F22.imprint","IMPRINT",FACE,{"disambiguationData":[TD([[makeQuery(id+"F22.imprint","IMPRINT",EDGE,{"derivedFrom":subQ0}),1.0]])]});}
            var Q16;
            {var subQ3=sQuery(id+"F22.wireOp",EDGE,"E99");Q16=makeQuery(id+"F22.imprint","IMPRINT",FACE,{"disambiguationData":[TD([[makeQuery(id+"F22.imprint","IMPRINT",EDGE,{"derivedFrom":subQ3}),-1.0]])]});}
            var Q17;
            {var subQ0=sQuery(id+"F22.wireOp",EDGE,"E106");var subQ1=sQuery(id+"F22.wireOp",EDGE,"E87");var subQ2=makeQuery(id+"F22.imprint","INTERSECT",VERTEX,{"derivedFrom":[subQ1,subQ0]});Q17=makeQuery(id+"F22.imprint","IMPRINT",FACE,{"disambiguationData":[TD([[makeQuery(id+"F22.imprint","IMPRINT",EDGE,{"disambiguationData":[TD([[subQ2,-1.0]])],"derivedFrom":subQ1}),1.0]])]});}
            var Q18;
            {var subQ0=sQuery(id+"F22.wireOp",EDGE,"E95");var subQ1=sQuery(id+"F22.wireOp",EDGE,"E87");var subQ2=makeQuery(id+"F22.imprint","INTERSECT",VERTEX,{"derivedFrom":[subQ1,subQ0]});Q18=makeQuery(id+"F22.imprint","IMPRINT",FACE,{"disambiguationData":[TD([[makeQuery(id+"F22.imprint","IMPRINT",EDGE,{"disambiguationData":[TD([[subQ2,-1.0]])],"derivedFrom":subQ1}),1.0]])]});}
            var Q19;
            {var subQ1=sQuery(id+"F22.wireOp",EDGE,"E102");var subQ3=sQuery(id+"F22.wireOp",EDGE,"E106");var subQ4=makeQuery(id+"F22.imprint","INTERSECT",VERTEX,{"derivedFrom":[subQ1,subQ3]});Q19=makeQuery(id+"F22.imprint","IMPRINT",FACE,{"disambiguationData":[TD([[makeQuery(id+"F22.imprint","IMPRINT",EDGE,{"disambiguationData":[TD([[subQ4,1.0]])],"derivedFrom":subQ3}),-1.0]])]});}
            var Q20;
            {var subQ0=sQuery(id+"F22.wireOp",EDGE,"E85.9");var subQ1=sQuery(id+"F22.wireOp",EDGE,"E85.5");var subQ2=makeQuery(id+"F22.imprint","INTERSECT",VERTEX,{"derivedFrom":[subQ1,subQ0]});Q20=makeQuery(id+"F22.imprint","IMPRINT",FACE,{"disambiguationData":[TD([[makeQuery(id+"F22.imprint","IMPRINT",EDGE,{"disambiguationData":[TD([[subQ2,-1.0]])],"derivedFrom":subQ1}),1.0]])]});}
            var Q21;
            {var subQ0=sQuery(id+"F22.wireOp",EDGE,"E93");var subQ3=sQuery(id+"F22.wireOp",EDGE,"E108");var subQ5=makeQuery(id+"F22.imprint","INTERSECT",VERTEX,{"derivedFrom":[subQ0,subQ3]});Q21=makeQuery(id+"F22.imprint","IMPRINT",FACE,{"disambiguationData":[TD([[makeQuery(id+"F22.imprint","IMPRINT",EDGE,{"disambiguationData":[TD([[subQ5,1.0]])],"derivedFrom":subQ3}),1.0]])]});}
            var Q22;
            {var subQ0=sQuery(id+"F22.wireOp",EDGE,"E107");var subQ1=sQuery(id+"F22.wireOp",EDGE,"E88");var subQ2=makeQuery(id+"F22.imprint","INTERSECT",VERTEX,{"derivedFrom":[subQ1,subQ0]});Q22=makeQuery(id+"F22.imprint","IMPRINT",FACE,{"disambiguationData":[TD([[makeQuery(id+"F22.imprint","IMPRINT",EDGE,{"disambiguationData":[TD([[subQ2,-1.0]])],"derivedFrom":subQ1}),-1.0]])]});}
            var Q23;
            {var subQ0=sQuery(id+"F22.wireOp",EDGE,"E90");var subQ1=sQuery(id+"F22.wireOp",EDGE,"E86");var subQ2=makeQuery(id+"F22.imprint","INTERSECT",VERTEX,{"derivedFrom":[subQ1,subQ0]});Q23=makeQuery(id+"F22.imprint","IMPRINT",FACE,{"disambiguationData":[TD([[makeQuery(id+"F22.imprint","IMPRINT",EDGE,{"disambiguationData":[TD([[subQ2,-1.0]])],"derivedFrom":subQ1}),1.0]])]});}
            var Q24;
            {var subQ3=sQuery(id+"F22.wireOp",EDGE,"E105");Q24=makeQuery(id+"F22.imprint","IMPRINT",FACE,{"disambiguationData":[TD([[makeQuery(id+"F22.imprint","IMPRINT",EDGE,{"derivedFrom":subQ3}),1.0]])]});}
            extrude(context, id + "F23", {"entities" : qUnion([Q0, Q1, Q2, Q3, Q4, Q5, Q6, Q7, Q8, Q9, Q10, Q11, Q12, Q13, Q14, Q15, Q16, Q17, Q18, Q19, Q20, Q21, Q22, Q23, Q24]), "operationType" : NewBodyOperationType.REMOVE, "oppositeDirection" : true, "depth" : 25 * mm, "offsetDistance" : 25 * mm});
        }
        {
            var Q0;
            Q0=makeQuery(id+"F3.opExtrude","CAP_EDGE",EDGE,{"disambiguationData":[OSD([sQuery(id+"F1.wireOp",EDGE,"E11.2")])],"isStart":true});
            var Q1;
            Q1=makeQuery(id+"F9.opFillet","BLEND_EDGE",EDGE,{"blendedFrom":[makeQuery(id+"F3.opExtrude","SWEPT_EDGE",EDGE,{"disambiguationData":[OSD([sQuery(id+"F1.wireOp",EDGE,"E11.2"),sQuery(id+"F1.wireOp",EDGE,"E11.3")])]}),makeQuery(id+"F7.boolean.opBoolean","MERGE",FACE,{"derivedFrom":[makeQuery(id+"F5.boolean.opBoolean","MERGE",FACE,{"derivedFrom":[makeQuery(id+"F2.opExtrude","CAP_FACE",FACE,{"disambiguationData":[OSD([sQuery(id+"F1.wireOp",EDGE,"E12.0"),sQuery(id+"F1.wireOp",EDGE,"E12.1"),sQuery(id+"F1.wireOp",EDGE,"E12.2"),sQuery(id+"F1.wireOp",EDGE,"E12.3")])],"isStart":true}),makeQuery(id+"F5.opExtrude","SWEPT_FACE",FACE,{"disambiguationData":[OSD([sQuery(id+"F4.wireOp",EDGE,"E20.bottom")])]})]}),makeQuery(id+"F7.opExtrude","SWEPT_FACE",FACE,{"disambiguationData":[OSD([sQuery(id+"F6.wireOp",EDGE,"E26")])]}),makeQuery(id+"F7.opExtrude","SWEPT_FACE",FACE,{"disambiguationData":[OSD([sQuery(id+"F6.wireOp",EDGE,"E31")])]})]})],"blendedInto":[makeQuery(id+"F7.boolean.opBoolean","MERGE",FACE,{"derivedFrom":[makeQuery(id+"F5.boolean.opBoolean","MERGE",FACE,{"derivedFrom":[makeQuery(id+"F2.opExtrude","CAP_FACE",FACE,{"disambiguationData":[OSD([sQuery(id+"F1.wireOp",EDGE,"E12.0"),sQuery(id+"F1.wireOp",EDGE,"E12.1"),sQuery(id+"F1.wireOp",EDGE,"E12.2"),sQuery(id+"F1.wireOp",EDGE,"E12.3")])],"isStart":true}),makeQuery(id+"F5.opExtrude","SWEPT_FACE",FACE,{"disambiguationData":[OSD([sQuery(id+"F4.wireOp",EDGE,"E20.bottom")])]})]}),makeQuery(id+"F7.opExtrude","SWEPT_FACE",FACE,{"disambiguationData":[OSD([sQuery(id+"F6.wireOp",EDGE,"E26")])]}),makeQuery(id+"F7.opExtrude","SWEPT_FACE",FACE,{"disambiguationData":[OSD([sQuery(id+"F6.wireOp",EDGE,"E31")])]})]})]});
            var Q2;
            {var subQ0=sQuery(id+"F1.wireOp",EDGE,"E11.3");Q2=makeQuery(id+"F5.boolean.opBoolean","SPLIT",EDGE,{"disambiguationData":[TD([makeQuery(id+"F3.opExtrude","SWEPT_FACE",FACE,{"disambiguationData":[OSD([sQuery(id+"F1.wireOp",EDGE,"E11.2")])]})])],"derivedFrom":makeQuery(id+"F3.opExtrude","CAP_EDGE",EDGE,{"disambiguationData":[OSD([subQ0])],"isStart":true})});}
            var Q3;
            Q3=makeQuery(id+"F9.opFillet","BLEND_EDGE",EDGE,{"blendedFrom":[makeQuery(id+"F3.opExtrude","SWEPT_EDGE",EDGE,{"disambiguationData":[OSD([sQuery(id+"F1.wireOp",EDGE,"E11.1"),sQuery(id+"F1.wireOp",EDGE,"E11.2")])]}),makeQuery(id+"F7.boolean.opBoolean","MERGE",FACE,{"derivedFrom":[makeQuery(id+"F5.boolean.opBoolean","MERGE",FACE,{"derivedFrom":[makeQuery(id+"F2.opExtrude","CAP_FACE",FACE,{"disambiguationData":[OSD([sQuery(id+"F1.wireOp",EDGE,"E12.0"),sQuery(id+"F1.wireOp",EDGE,"E12.1"),sQuery(id+"F1.wireOp",EDGE,"E12.2"),sQuery(id+"F1.wireOp",EDGE,"E12.3")])],"isStart":true}),makeQuery(id+"F5.opExtrude","SWEPT_FACE",FACE,{"disambiguationData":[OSD([sQuery(id+"F4.wireOp",EDGE,"E20.bottom")])]})]}),makeQuery(id+"F7.opExtrude","SWEPT_FACE",FACE,{"disambiguationData":[OSD([sQuery(id+"F6.wireOp",EDGE,"E26")])]}),makeQuery(id+"F7.opExtrude","SWEPT_FACE",FACE,{"disambiguationData":[OSD([sQuery(id+"F6.wireOp",EDGE,"E31")])]})]})],"blendedInto":[makeQuery(id+"F7.boolean.opBoolean","MERGE",FACE,{"derivedFrom":[makeQuery(id+"F5.boolean.opBoolean","MERGE",FACE,{"derivedFrom":[makeQuery(id+"F2.opExtrude","CAP_FACE",FACE,{"disambiguationData":[OSD([sQuery(id+"F1.wireOp",EDGE,"E12.0"),sQuery(id+"F1.wireOp",EDGE,"E12.1"),sQuery(id+"F1.wireOp",EDGE,"E12.2"),sQuery(id+"F1.wireOp",EDGE,"E12.3")])],"isStart":true}),makeQuery(id+"F5.opExtrude","SWEPT_FACE",FACE,{"disambiguationData":[OSD([sQuery(id+"F4.wireOp",EDGE,"E20.bottom")])]})]}),makeQuery(id+"F7.opExtrude","SWEPT_FACE",FACE,{"disambiguationData":[OSD([sQuery(id+"F6.wireOp",EDGE,"E26")])]}),makeQuery(id+"F7.opExtrude","SWEPT_FACE",FACE,{"disambiguationData":[OSD([sQuery(id+"F6.wireOp",EDGE,"E31")])]})]})]});
            var Q4;
            {var subQ0=sQuery(id+"F1.wireOp",EDGE,"E11.1");Q4=makeQuery(id+"F5.boolean.opBoolean","SPLIT",EDGE,{"disambiguationData":[TD([makeQuery(id+"F3.opExtrude","SWEPT_FACE",FACE,{"disambiguationData":[OSD([sQuery(id+"F1.wireOp",EDGE,"E11.2")])]})])],"derivedFrom":makeQuery(id+"F3.opExtrude","CAP_EDGE",EDGE,{"disambiguationData":[OSD([subQ0])],"isStart":true})});}
            var Q5;
            {var subQ0=sQuery(id+"F1.wireOp",EDGE,"E11.1");Q5=makeQuery(id+"F5.boolean.opBoolean","SPLIT",EDGE,{"disambiguationData":[TD([makeQuery(id+"F3.opExtrude","SWEPT_FACE",FACE,{"disambiguationData":[OSD([sQuery(id+"F1.wireOp",EDGE,"E11.0")])]})])],"derivedFrom":makeQuery(id+"F3.opExtrude","CAP_EDGE",EDGE,{"disambiguationData":[OSD([subQ0])],"isStart":true})});}
            var Q6;
            Q6=makeQuery(id+"F9.opFillet","BLEND_EDGE",EDGE,{"blendedFrom":[makeQuery(id+"F3.opExtrude","SWEPT_EDGE",EDGE,{"disambiguationData":[OSD([sQuery(id+"F1.wireOp",EDGE,"E11.0"),sQuery(id+"F1.wireOp",EDGE,"E11.1")])]}),makeQuery(id+"F7.boolean.opBoolean","MERGE",FACE,{"derivedFrom":[makeQuery(id+"F5.boolean.opBoolean","MERGE",FACE,{"derivedFrom":[makeQuery(id+"F2.opExtrude","CAP_FACE",FACE,{"disambiguationData":[OSD([sQuery(id+"F1.wireOp",EDGE,"E12.0"),sQuery(id+"F1.wireOp",EDGE,"E12.1"),sQuery(id+"F1.wireOp",EDGE,"E12.2"),sQuery(id+"F1.wireOp",EDGE,"E12.3")])],"isStart":true}),makeQuery(id+"F5.opExtrude","SWEPT_FACE",FACE,{"disambiguationData":[OSD([sQuery(id+"F4.wireOp",EDGE,"E20.bottom")])]})]}),makeQuery(id+"F7.opExtrude","SWEPT_FACE",FACE,{"disambiguationData":[OSD([sQuery(id+"F6.wireOp",EDGE,"E26")])]}),makeQuery(id+"F7.opExtrude","SWEPT_FACE",FACE,{"disambiguationData":[OSD([sQuery(id+"F6.wireOp",EDGE,"E31")])]})]})],"blendedInto":[makeQuery(id+"F7.boolean.opBoolean","MERGE",FACE,{"derivedFrom":[makeQuery(id+"F5.boolean.opBoolean","MERGE",FACE,{"derivedFrom":[makeQuery(id+"F2.opExtrude","CAP_FACE",FACE,{"disambiguationData":[OSD([sQuery(id+"F1.wireOp",EDGE,"E12.0"),sQuery(id+"F1.wireOp",EDGE,"E12.1"),sQuery(id+"F1.wireOp",EDGE,"E12.2"),sQuery(id+"F1.wireOp",EDGE,"E12.3")])],"isStart":true}),makeQuery(id+"F5.opExtrude","SWEPT_FACE",FACE,{"disambiguationData":[OSD([sQuery(id+"F4.wireOp",EDGE,"E20.bottom")])]})]}),makeQuery(id+"F7.opExtrude","SWEPT_FACE",FACE,{"disambiguationData":[OSD([sQuery(id+"F6.wireOp",EDGE,"E26")])]}),makeQuery(id+"F7.opExtrude","SWEPT_FACE",FACE,{"disambiguationData":[OSD([sQuery(id+"F6.wireOp",EDGE,"E31")])]})]})]});
            var Q7;
            {var subQ0=sQuery(id+"F1.wireOp",EDGE,"E11.0");Q7=makeQuery(id+"F7.boolean.opBoolean","SPLIT",EDGE,{"disambiguationData":[TD([makeQuery(id+"F3.opExtrude","SWEPT_FACE",FACE,{"disambiguationData":[OSD([sQuery(id+"F1.wireOp",EDGE,"E11.1")])]})])],"derivedFrom":makeQuery(id+"F3.opExtrude","CAP_EDGE",EDGE,{"disambiguationData":[OSD([subQ0])],"isStart":true})});}
            var Q8;
            {var subQ0=sQuery(id+"F1.wireOp",EDGE,"E11.0");Q8=makeQuery(id+"F7.boolean.opBoolean","SPLIT",EDGE,{"disambiguationData":[TD([makeQuery(id+"F7.opExtrude","SWEPT_FACE",FACE,{"disambiguationData":[OSD([sQuery(id+"F6.wireOp",EDGE,"E23"),sQuery(id+"F6.wireOp",EDGE,"E27")])]})])],"derivedFrom":makeQuery(id+"F3.opExtrude","CAP_EDGE",EDGE,{"disambiguationData":[OSD([subQ0])],"isStart":true})});}
            var Q9;
            {var subQ0=sQuery(id+"F1.wireOp",EDGE,"E11.0");Q9=makeQuery(id+"F7.boolean.opBoolean","SPLIT",EDGE,{"disambiguationData":[TD([makeQuery(id+"F3.opExtrude","SWEPT_FACE",FACE,{"disambiguationData":[OSD([sQuery(id+"F1.wireOp",EDGE,"E11.3")])]})])],"derivedFrom":makeQuery(id+"F3.opExtrude","CAP_EDGE",EDGE,{"disambiguationData":[OSD([subQ0])],"isStart":true})});}
            var Q10;
            Q10=makeQuery(id+"F9.opFillet","BLEND_EDGE",EDGE,{"blendedFrom":[makeQuery(id+"F3.opExtrude","SWEPT_EDGE",EDGE,{"disambiguationData":[OSD([sQuery(id+"F1.wireOp",EDGE,"E11.0"),sQuery(id+"F1.wireOp",EDGE,"E11.3")])]}),makeQuery(id+"F7.boolean.opBoolean","MERGE",FACE,{"derivedFrom":[makeQuery(id+"F5.boolean.opBoolean","MERGE",FACE,{"derivedFrom":[makeQuery(id+"F2.opExtrude","CAP_FACE",FACE,{"disambiguationData":[OSD([sQuery(id+"F1.wireOp",EDGE,"E12.0"),sQuery(id+"F1.wireOp",EDGE,"E12.1"),sQuery(id+"F1.wireOp",EDGE,"E12.2"),sQuery(id+"F1.wireOp",EDGE,"E12.3")])],"isStart":true}),makeQuery(id+"F5.opExtrude","SWEPT_FACE",FACE,{"disambiguationData":[OSD([sQuery(id+"F4.wireOp",EDGE,"E20.bottom")])]})]}),makeQuery(id+"F7.opExtrude","SWEPT_FACE",FACE,{"disambiguationData":[OSD([sQuery(id+"F6.wireOp",EDGE,"E26")])]}),makeQuery(id+"F7.opExtrude","SWEPT_FACE",FACE,{"disambiguationData":[OSD([sQuery(id+"F6.wireOp",EDGE,"E31")])]})]})],"blendedInto":[makeQuery(id+"F7.boolean.opBoolean","MERGE",FACE,{"derivedFrom":[makeQuery(id+"F5.boolean.opBoolean","MERGE",FACE,{"derivedFrom":[makeQuery(id+"F2.opExtrude","CAP_FACE",FACE,{"disambiguationData":[OSD([sQuery(id+"F1.wireOp",EDGE,"E12.0"),sQuery(id+"F1.wireOp",EDGE,"E12.1"),sQuery(id+"F1.wireOp",EDGE,"E12.2"),sQuery(id+"F1.wireOp",EDGE,"E12.3")])],"isStart":true}),makeQuery(id+"F5.opExtrude","SWEPT_FACE",FACE,{"disambiguationData":[OSD([sQuery(id+"F4.wireOp",EDGE,"E20.bottom")])]})]}),makeQuery(id+"F7.opExtrude","SWEPT_FACE",FACE,{"disambiguationData":[OSD([sQuery(id+"F6.wireOp",EDGE,"E26")])]}),makeQuery(id+"F7.opExtrude","SWEPT_FACE",FACE,{"disambiguationData":[OSD([sQuery(id+"F6.wireOp",EDGE,"E31")])]})]})]});
            var Q11;
            {var subQ0=sQuery(id+"F1.wireOp",EDGE,"E11.3");Q11=makeQuery(id+"F5.boolean.opBoolean","SPLIT",EDGE,{"disambiguationData":[TD([makeQuery(id+"F3.opExtrude","SWEPT_FACE",FACE,{"disambiguationData":[OSD([sQuery(id+"F1.wireOp",EDGE,"E11.0")])]})])],"derivedFrom":makeQuery(id+"F3.opExtrude","CAP_EDGE",EDGE,{"disambiguationData":[OSD([subQ0])],"isStart":true})});}
            fillet(context, id + "F24", {"entities" : qUnion([Q0, Q1, Q2, Q3, Q4, Q5, Q6, Q7, Q8, Q9, Q10, Q11]), "radius" : 2 * mm, "tangentPropagation" : true, "allowEdgeOverflow" : false});
        }
    });
